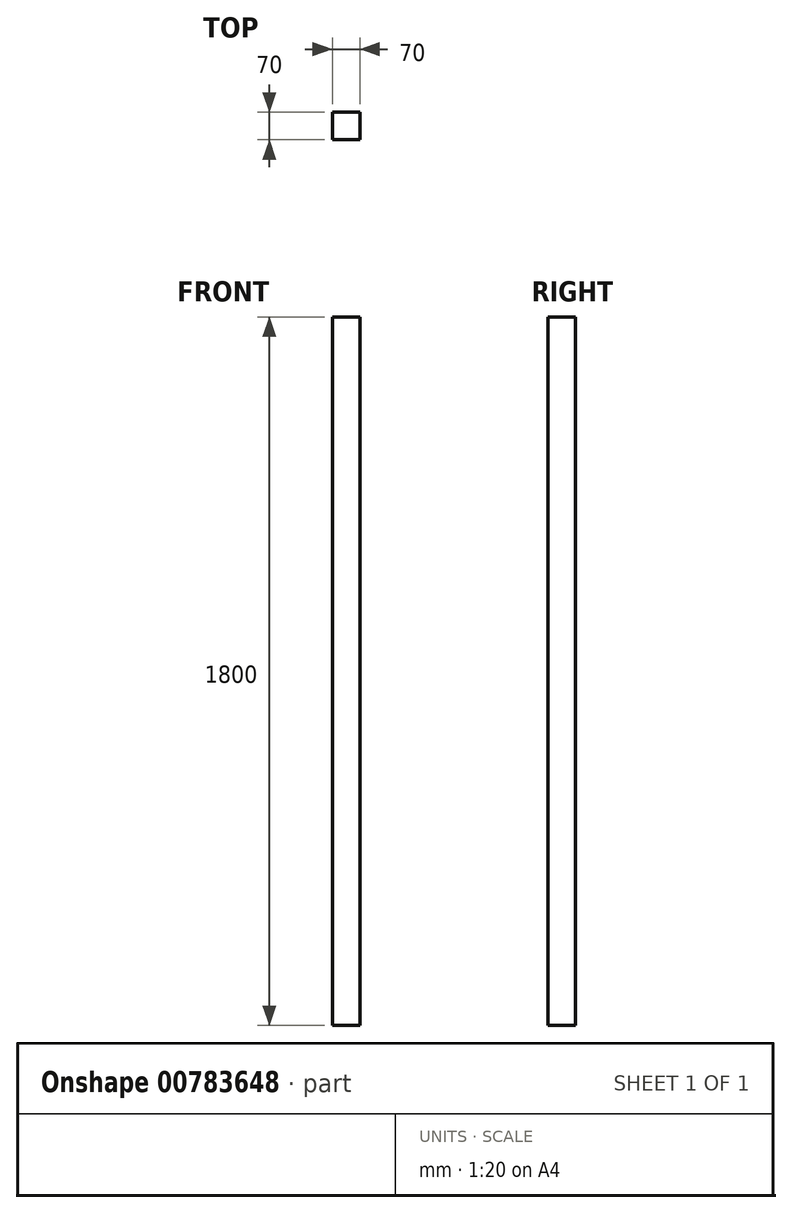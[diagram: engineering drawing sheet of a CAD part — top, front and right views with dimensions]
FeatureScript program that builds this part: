
annotation { "Feature Type Name" : "Feature", "Feature Type Description" : "" }
export const myFeature = defineFeature(function(context is Context, id is Id, definition is map)
    precondition{}
    {
        {
            var Q0;
            Q0=qCreatedBy(makeId("Top.planeOp"),FACE);
            var sketch = newSketch(context, id + "F0", { "sketchPlane" : qUnion([Q0])});
            skLineSegment(sketch, "E0.bottom", {"start": v(35, 35) * mm, "end": v(-35, 35) * mm});
            skLineSegment(sketch, "E0.top", {"start": v(35, -35) * mm, "end": v(-35, -35) * mm});
            skLineSegment(sketch, "E0.left", {"start": v(35, 35) * mm, "end": v(35, -35) * mm});
            skLineSegment(sketch, "E0.right", {"start": v(-35, 35) * mm, "end": v(-35, -35) * mm});
            skPoint(sketch, "E0.middle", {"position": v(0, 0) * mm});
            skSolve(sketch);
        }
        {
            var Q0;
            Q0=makeQuery(id+"F0.imprint","IMPRINT",FACE,{"disambiguationData":[TD([[makeQuery(id+"F0.imprint","IMPRINT",EDGE,{"derivedFrom":sQuery(id+"F0.wireOp",EDGE,"E0.bottom")}),1.0]])]});
            extrude(context, id + "F1", {"entities" : qUnion([Q0]), "depth" : 1800 * mm, "offsetDistance" : 25 * mm});
        }
    });
